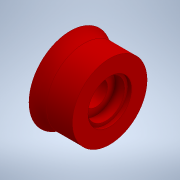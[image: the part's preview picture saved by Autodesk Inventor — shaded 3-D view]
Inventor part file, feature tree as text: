
AUTODESK INVENTOR PART (.ipt)
format: ipt  version: 2020 (Build 240168000, 168)  size: 228,352 bytes
history: native  units: mm
features: extrude x5, sketch x5, other x3, fillet x2, projected_geometry x1
ambient origin geometry x8: Origin, YZ Plane, XZ Plane, XY Plane, X Axis, Y Axis, Z Axis, Center Point
bodies: Solid1 (feature_tree)
feature tree (16):
  other  "WeaponMountBasePlateV1.ipt"
  extrude  "Extrusion1"  Depth=10.0mm
  extrude  "Extrusion2"  TaperAngle=0.0deg  [1 undecoded]
  extrude  "Extrusion3"  Depth=0.75mm
  fillet  "Fillet1"  [1 undecoded]
  fillet  "Fillet2"  Radius=7.3mm
  extrude  "Extrusion4"  TaperAngle=0.0deg  [1 undecoded]
  extrude  "Extrusion5"  Depth=5.0mm
  other  "Solid1::WeaponMountBasePlateV1.ipt"
  other  "TaggingFeature1"
  sketch  "Sketch2"  dims[d0=10.0mm d2=14.45mm]
  sketch  "Sketch3"  dims[d3=10.0mm d4=0.0mm]
  sketch  "Sketch4"  dims[d5=8.45mm d6=0.75mm d7=0.0mm d8=7.3mm]
  projected_geometry  "Projected Loop1"
  sketch  "Sketch5"  dims[d9=1.9mm d10=0.0mm]
  sketch  "Sketch6"  dims[d11=1.5mm d12=5.0mm d13=4.5mm d14=5.0mm d15=0.0mm d16=10.0mm d17=0.0mm]
note: 3 required parameter values undecoded (feature->parameter linkage not recoverable at this tier; creation-order binding heuristic only, values carry confidence <= 0.55)
